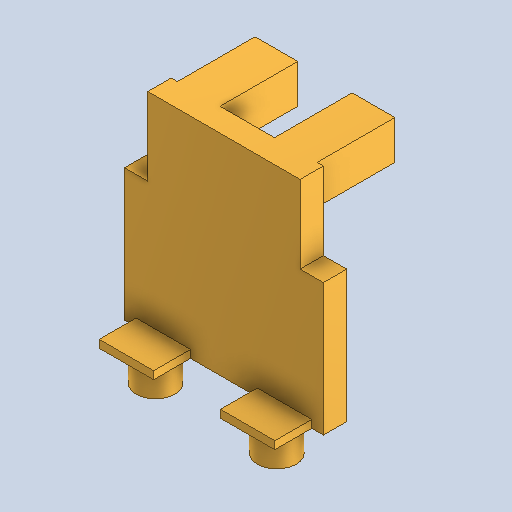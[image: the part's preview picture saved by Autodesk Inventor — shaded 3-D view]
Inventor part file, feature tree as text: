
AUTODESK INVENTOR PART (.ipt)
format: ipt  version: 2025 (Build 290162010, 162A)  size: 213,504 bytes
history: native  units: mm
features: extrude x4, sketch x4
ambient origin geometry x8: Origin, YZ Plane, XZ Plane, XY Plane, X Axis, Y Axis, Z Axis, Center Point
bodies: Volumenkörper1 (feature_tree)
feature tree (8):
  extrude  "Extrusion1"  Depth=3.0mm TaperAngle=0.0deg
  extrude  "Extrusion2"  Depth=5.0mm
  sketch  "Skizze5"  dims[d31=4.0mm d32=0.0mm d43=7.0mm]
  extrude  "Extrusion4"  Depth=7.0mm
  extrude  "Extrusion5"  Depth=5.0mm
  sketch  "Skizze1"  dims[d1=27.0mm d7=3.0mm d8=0.0mm]
  sketch  "Skizze3"  dims[d9=25.6mm d29=5.0mm]
  sketch  "Skizze6"  dims[d50=10.0mm d51=0.0mm d54=5.0mm d55=18.0mm d56=3.0mm d57=10.0mm d58=3.0mm d59=10.0mm d60=5.0mm d62=5.0mm d64=5.0mm d65=7.0mm d66=1.0mm d67=7.0mm d68=1.0mm d69=7.75mm d70=0.0mm d71=5.0mm d72=0.0mm d73=1.0mm]
